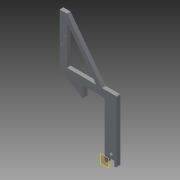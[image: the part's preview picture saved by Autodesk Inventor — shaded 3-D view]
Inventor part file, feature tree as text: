
AUTODESK INVENTOR PART (.ipt)
format: ipt  version: 2013 (Build 170138000, 138)  size: 206,848 bytes
history: native  units: in
note: dims shown in document units (in); Inventor stores cm internally (conversion verified against a paired STEP export)
features: fillet x6, sketch x3, extrude x3, plane x1
ambient origin geometry x8: Origin, YZ Plane, XZ Plane, XY Plane, X Axis, Y Axis, Z Axis, Center Point
feature tree (13):
  plane  "Work Plane1"
  sketch  "Sketch2"  dims[d0=0.25in d1=0.5in]
  extrude  "Extrusion4"  Depth=0.5in
  extrude  "Extrusion5"  Depth=0.25in
  fillet  "Fillet2"  Radius=6.375in
  fillet  "Fillet3"  Radius=0.3765in
  fillet  "Fillet4"  Radius=0.5in
  fillet  "Fillet5"  Radius=0.375in
  extrude  "Extrusion7"  Depth=0.75in
  fillet  "Fillet6"  Radius=2.15in
  fillet  "Fillet7"  Radius=1.25in
  sketch  "Sketch5"  dims[d8=5.875in d9=0.75in d12=2.15in d13=1.25in d14=2.0in d15=0.75in d18=5.0in d19=3.0in d24=0.125in d25=0.573in d26=2.6125in d27=0.125in d29=3.5185in d32=0.175in d33=0.75in d34=4.8333in d36=3.0in d37=0.75in d38=0.75in d39=3.0in d40=3.0in d41=0.75in d42=0.375in d43=0.0in d44=0.375in d45=0.0in d50=0.0034in d51=0.5in d52=0.125in d53=0.125in d54=0.125in d55=0.125in d56=0.5in d57=0.375in d58=0.0in d59=0.125in d60=0.25in]
  sketch  "Sketch4"  dims[d2=0.75in d3=0.25in d4=6.375in d5=0.3765in d6=0.5in d7=0.375in]
